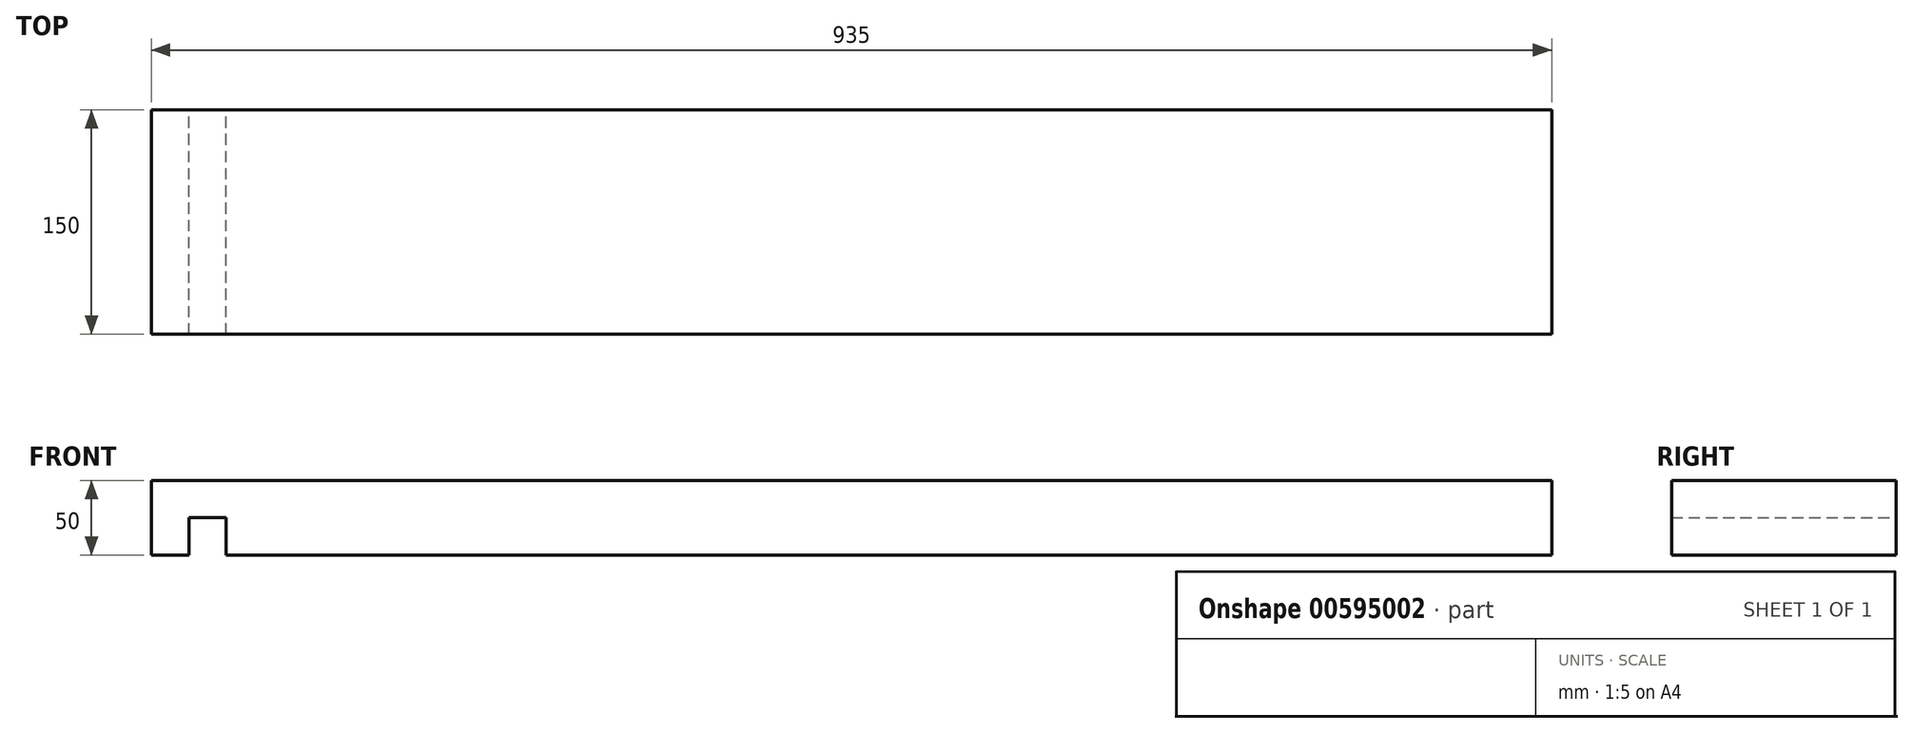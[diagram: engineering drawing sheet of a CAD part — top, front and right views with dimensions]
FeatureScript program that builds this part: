
annotation { "Feature Type Name" : "Feature", "Feature Type Description" : "" }
export const myFeature = defineFeature(function(context is Context, id is Id, definition is map)
    precondition{}
    {
        {
            var Q0;
            Q0=qCreatedBy(makeId("Front.planeOp"),FACE);
            var sketch = newSketch(context, id + "F0", { "sketchPlane" : qUnion([Q0])});
            skLineSegment(sketch, "E0", {"start": v(68.17, 50) * mm, "end": v(68.17, 0) * mm});
            skLineSegment(sketch, "E1", {"start": v(68.17, 0) * mm, "end": v(-6.83, 0) * mm});
            skLineSegment(sketch, "E2", {"start": v(-6.83, 0) * mm, "end": v(-6.83, 25) * mm});
            skLineSegment(sketch, "E3", {"start": v(-6.83, 25) * mm, "end": v(-56.83, 25) * mm});
            skLineSegment(sketch, "E4", {"start": v(-56.83, 25) * mm, "end": v(-56.83, 0) * mm});
            skLineSegment(sketch, "E5", {"start": v(-56.83, 25) * mm, "end": v(-56.83, 50) * mm});
            skLineSegment(sketch, "E6", {"start": v(-56.83, 50) * mm, "end": v(68.17, 50) * mm});
            skLineSegment(sketch, "E7", {"start": v(-31.83, 0) * mm, "end": v(-56.83, 0) * mm});
            skLineSegment(sketch, "E8", {"start": v(-31.83, 0) * mm, "end": v(-31.83, 50) * mm});
            skLineSegment(sketch, "E9", {"start": v(-56.83, 50) * mm, "end": v(-31.83, 50) * mm});
            skSolve(sketch);
        }
        {
            var Q0;
            Q0 = qSketchRegion(id + "F0", true);
            extrude(context, id + "F1", {"entities" : qUnion([Q0]), "depth" : 150 * mm, "offsetDistance" : 25 * mm});
        }
        {
            var Q0;
            Q0 = qSketchRegion(id + "F0", true);
            extrude(context, id + "F2", {"entities" : qUnion([Q0]), "operationType" : NewBodyOperationType.ADD, "depth" : 150 * mm, "offsetDistance" : 25 * mm});
        }
        {
            var Q0;
            Q0=makeQuery(id+"F1.opExtrude","SWEPT_FACE",FACE,{"disambiguationData":[OSD([sQuery(id+"F0.wireOp",EDGE,"E0")])]});
            var sketch = newSketch(context, id + "F3", { "sketchPlane" : qUnion([Q0])});
            skLineSegment(sketch, "E10.bottom", {"start": v(0, 0) * mm, "end": v(-150, 0) * mm});
            skLineSegment(sketch, "E10.top", {"start": v(0, 50) * mm, "end": v(-150, 50) * mm});
            skLineSegment(sketch, "E10.left", {"start": v(0, 0) * mm, "end": v(0, 50) * mm});
            skLineSegment(sketch, "E10.right", {"start": v(-150, 0) * mm, "end": v(-150, 50) * mm});
            skSolve(sketch);
        }
        {
            var Q0;
            Q0 = qSketchRegion(id + "F3", true);
            extrude(context, id + "F4", {"entities" : qUnion([Q0]), "operationType" : NewBodyOperationType.ADD, "depth" : 810 * mm, "offsetDistance" : 25 * mm});
        }
    });
